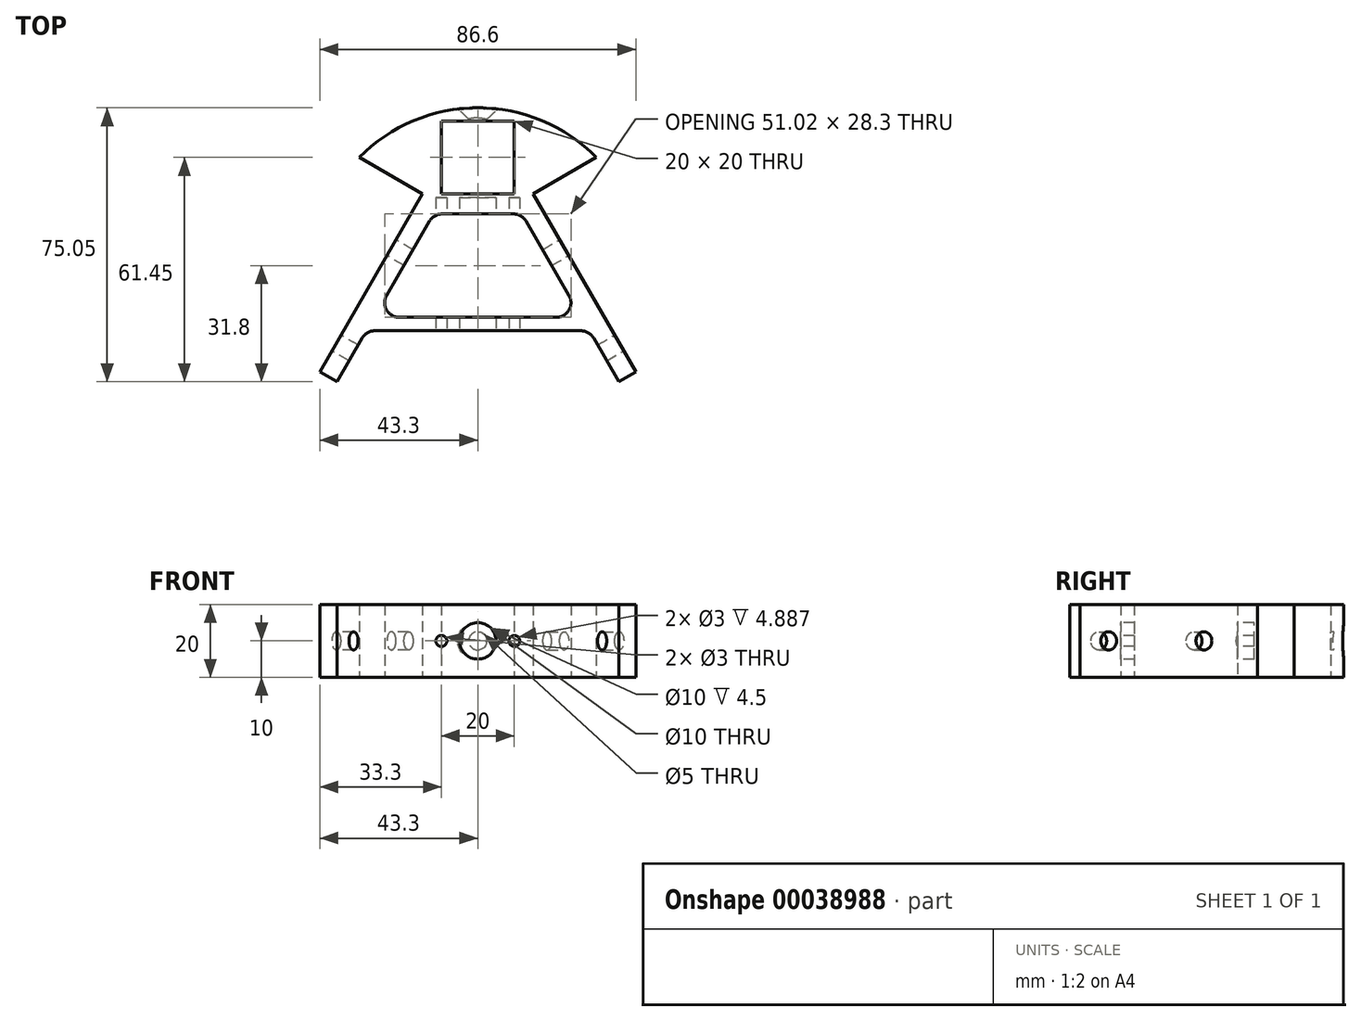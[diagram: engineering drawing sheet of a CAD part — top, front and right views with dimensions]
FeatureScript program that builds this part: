
annotation { "Feature Type Name" : "Feature", "Feature Type Description" : "" }
export const myFeature = defineFeature(function(context is Context, id is Id, definition is map)
    precondition{}
    {
        {
            var Q0;
            Q0=qCreatedBy(makeId("Top.planeOp"),FACE);
            var sketch = newSketch(context, id + "F0", { "sketchPlane" : qUnion([Q0])});
            skLineSegment(sketch, "E0", {"start": v(0, 0) * mm, "end": v(0, -10) * mm, "construction": true});
            skLineSegment(sketch, "E1.bottom", {"start": v(10, -10) * mm, "end": v(0, -10) * mm});
            skLineSegment(sketch, "E1.top", {"start": v(10, 10) * mm, "end": v(0, 10) * mm});
            skLineSegment(sketch, "E1.left", {"start": v(10, -10) * mm, "end": v(10, 10) * mm});
            skPoint(sketch, "E1.middle", {"position": v(0, 0) * mm});
            skLineSegment(sketch, "E2", {"start": v(0, 0) * mm, "end": v(0, 10) * mm, "construction": true});
            skPoint(sketch, "E1.right.start.orphan", {"position": v(-10, -10) * mm});
            skPoint(sketch, "E3.orphan", {"position": v(-10, 10) * mm});
            skLineSegment(sketch, "E4", {"start": v(0, -10) * mm, "end": v(0, -72.74) * mm, "construction": true});
            skLineSegment(sketch, "E5", {"start": v(15.16, -10) * mm, "end": v(43.3, -58.75) * mm});
            skLineSegment(sketch, "E6", {"start": v(43.3, -58.75) * mm, "end": v(60.63, -48.75) * mm, "construction": true});
            skLineSegment(sketch, "E7", {"start": v(60.63, -48.75) * mm, "end": v(32.48, 0) * mm, "construction": true});
            skLineSegment(sketch, "E8", {"start": v(0, 10) * mm, "end": v(0, 13.6) * mm});
            skLineSegment(sketch, "E9", {"start": v(0, 13.6) * mm, "end": v(-73.6, 13.6) * mm, "construction": true});
            skLineSegment(sketch, "E10", {"start": v(43.3, -58.75) * mm, "end": v(38.63, -61.45) * mm});
            skLineSegment(sketch, "E11", {"start": v(0, -10) * mm, "end": v(0, -10) * mm});
            skArc(sketch, "E12", {"start": v(0, 13.6) * mm, "mid": v(17.6, 10.06) * mm, "end": v(32.48, 0) * mm});
            skLineSegment(sketch, "E13", {"start": v(15.16, -10) * mm, "end": v(32.48, 0) * mm});
            skLineSegment(sketch, "E14", {"start": v(38.63, -61.45) * mm, "end": v(31.73, -49.5) * mm});
            skLineSegment(sketch, "E15", {"start": v(28.27, -47.5) * mm, "end": v(0, -47.5) * mm});
            skLineSegment(sketch, "E16", {"start": v(0, -47.5) * mm, "end": v(0, -43.8) * mm});
            skLineSegment(sketch, "E17", {"start": v(0, -43.8) * mm, "end": v(21.51, -43.8) * mm});
            skLineSegment(sketch, "E18", {"start": v(24.97, -37.8) * mm, "end": v(13.25, -17.5) * mm});
            skLineSegment(sketch, "E19", {"start": v(9.8, -15.5) * mm, "end": v(0, -15.5) * mm});
            skLineSegment(sketch, "E20", {"start": v(0, -15.5) * mm, "end": v(0, -10) * mm});
            skPoint(sketch, "E21.visualSharp", {"position": v(12.1, -15.5) * mm});
            skArc(sketch, "E21.filletArc", {"start": v(13.25, -17.5) * mm, "mid": v(11.8, -16.04) * mm, "end": v(9.8, -15.5) * mm});
            skPoint(sketch, "E22.visualSharp", {"position": v(28.44, -43.8) * mm});
            skArc(sketch, "E22.filletArc", {"start": v(21.51, -43.8) * mm, "mid": v(24.97, -41.8) * mm, "end": v(24.97, -37.8) * mm});
            skPoint(sketch, "E23.visualSharp", {"position": v(30.57, -47.5) * mm});
            skArc(sketch, "E23.filletArc", {"start": v(31.73, -49.5) * mm, "mid": v(30.27, -48.04) * mm, "end": v(28.27, -47.5) * mm});
            skSolve(sketch);
        }
        {
            var Q0;
            Q0 = qSketchRegion(id + "F0", true);
            extrude(context, id + "F1", {"entities" : qUnion([Q0]), "depth" : 20 * mm});
        }
        {
            var Q0;
            Q0=makeQuery(id+"F1.opExtrude","SWEPT_FACE",FACE,{"disambiguationData":[OSD([sQuery(id+"F0.wireOp",EDGE,"E5")])]});
            var sketch = newSketch(context, id + "F2", { "sketchPlane" : qUnion([Q0])});
            skCircle(sketch, "E24", {"center": v(-63.4, 10) * mm, "radius": 2.5 * mm});
            skCircle(sketch, "E25", {"center": v(-33.25, 10) * mm, "radius": 2.5 * mm});
            skLineSegment(sketch, "E26", {"start": v(-33.25, 10) * mm, "end": v(-63.4, 10) * mm, "construction": true});
            skLineSegment(sketch, "E27", {"start": v(-72.53, 10) * mm, "end": v(-63.4, 10) * mm, "construction": true});
            skSolve(sketch);
        }
        {
            var Q0;
            Q0 = qSketchRegion(id + "F2", true);
            extrude(context, id + "F3", {"entities" : qUnion([Q0]), "operationType" : NewBodyOperationType.REMOVE, "oppositeDirection" : true, "depth" : 25 * mm});
        }
        {
            var Q0;
            Q0=makeQuery(id+"F1.opExtrude","SWEPT_FACE",FACE,{"disambiguationData":[OSD([sQuery(id+"F0.wireOp",EDGE,"E15")])]});
            var sketch = newSketch(context, id + "F4", { "sketchPlane" : qUnion([Q0])});
            skCircle(sketch, "E28", {"center": v(0, 10) * mm, "radius": 5 * mm});
            skCircle(sketch, "E29", {"center": v(10, 10) * mm, "radius": 1.5 * mm});
            skLineSegment(sketch, "E30", {"start": v(0, 10) * mm, "end": v(10, 10) * mm, "construction": true});
            skSolve(sketch);
        }
        {
            var Q0;
            Q0 = qSketchRegion(id + "F4", true);
            extrude(context, id + "F5", {"entities" : qUnion([Q0]), "operationType" : NewBodyOperationType.REMOVE, "oppositeDirection" : true, "depth" : 36.5 * mm});
        }
        {
            var Q0;
            Q0=makeQuery(id+"F1.opExtrude","SWEPT_FACE",FACE,{"disambiguationData":[OSD([sQuery(id+"F0.wireOp",EDGE,"E1.top")])]});
            var sketch = newSketch(context, id + "F6", { "sketchPlane" : qUnion([Q0])});
            skCircle(sketch, "E31", {"center": v(0, 10) * mm, "radius": 2.5 * mm});
            skSolve(sketch);
        }
        {
            var Q0;
            {var subQ0=sQuery(id+"F6.wireOp",EDGE,"E31");var subQ1=makeQuery(id+"F1.opExtrude","SWEPT_EDGE",EDGE,{"disambiguationData":[OSD([sQuery(id+"F0.wireOp",EDGE,"E1.top"),sQuery(id+"F0.wireOp",EDGE,"E8")])]});var subQ2=makeQuery(id+"F6.imprint","INTERSECT",VERTEX,{"disambiguationData":[OD(0.0)],"derivedFrom":[subQ1,subQ0]});Q0=makeQuery(id+"F6.imprint","IMPRINT",FACE,{"disambiguationData":[TD([[makeQuery(id+"F6.imprint","IMPRINT",EDGE,{"disambiguationData":[TD([[subQ2,1.0]])],"derivedFrom":subQ0}),1.0]])]});}
            var Q1;
            {var subQ0=sQuery(id+"F6.wireOp",EDGE,"E31");var subQ1=makeQuery(id+"F1.opExtrude","SWEPT_EDGE",EDGE,{"disambiguationData":[OSD([sQuery(id+"F0.wireOp",EDGE,"E1.top"),sQuery(id+"F0.wireOp",EDGE,"E8")])]});var subQ2=makeQuery(id+"F6.imprint","INTERSECT",VERTEX,{"disambiguationData":[OD(0.0)],"derivedFrom":[subQ1,subQ0]});Q1=makeQuery(id+"F6.imprint","IMPRINT",FACE,{"disambiguationData":[TD([[makeQuery(id+"F6.imprint","IMPRINT",EDGE,{"disambiguationData":[TD([[subQ2,-1.0]])],"derivedFrom":subQ0}),1.0]])]});}
            extrude(context, id + "F7", {"entities" : qUnion([Q0, Q1]), "operationType" : NewBodyOperationType.REMOVE, "oppositeDirection" : true, "depth" : 25 * mm});
        }
        {
            var Q0;
            Q0=makeQuery(id+"F7.boolean.opBoolean","INTERSECT",EDGE,{"derivedFrom":[makeQuery(id+"F1.opExtrude","SWEPT_FACE",FACE,{"disambiguationData":[OSD([sQuery(id+"F0.wireOp",EDGE,"E12")])]}),makeQuery(id+"F7.opExtrude","SWEPT_FACE",FACE,{"disambiguationData":[OSD([sQuery(id+"F6.wireOp",EDGE,"E31")])]})]});
            chamfer(context, id + "F8", {"entities" : qUnion([Q0]), "width" : 3 * mm, "tangentPropagation" : true});
        }
        {
            var Q0;
            Q0=makeQuery(id+"F1.opExtrude","SWEPT_BODY",BODY,{"disambiguationData":[OSD([sQuery(id+"F0.wireOp",EDGE,"E1.bottom"),sQuery(id+"F0.wireOp",EDGE,"E1.top"),sQuery(id+"F0.wireOp",EDGE,"E1.left"),sQuery(id+"F0.wireOp",EDGE,"E5"),sQuery(id+"F0.wireOp",EDGE,"E8"),sQuery(id+"F0.wireOp",EDGE,"E10"),sQuery(id+"F0.wireOp",EDGE,"E12"),sQuery(id+"F0.wireOp",EDGE,"E13"),sQuery(id+"F0.wireOp",EDGE,"E14"),sQuery(id+"F0.wireOp",EDGE,"E15"),sQuery(id+"F0.wireOp",EDGE,"E16"),sQuery(id+"F0.wireOp",EDGE,"E17"),sQuery(id+"F0.wireOp",EDGE,"E18"),sQuery(id+"F0.wireOp",EDGE,"E19"),sQuery(id+"F0.wireOp",EDGE,"E20"),sQuery(id+"F0.wireOp",EDGE,"E21.filletArc"),sQuery(id+"F0.wireOp",EDGE,"E22.filletArc"),sQuery(id+"F0.wireOp",EDGE,"E23.filletArc")])]});
            var Q1;
            Q1=qCreatedBy(makeId("Right.planeOp"),FACE);
            mirror(context, id + "F9", {"operationType" : NewBodyOperationType.ADD, "entities" : qUnion([Q0]), "mirrorPlane" : qUnion([Q1])});
        }
    });
